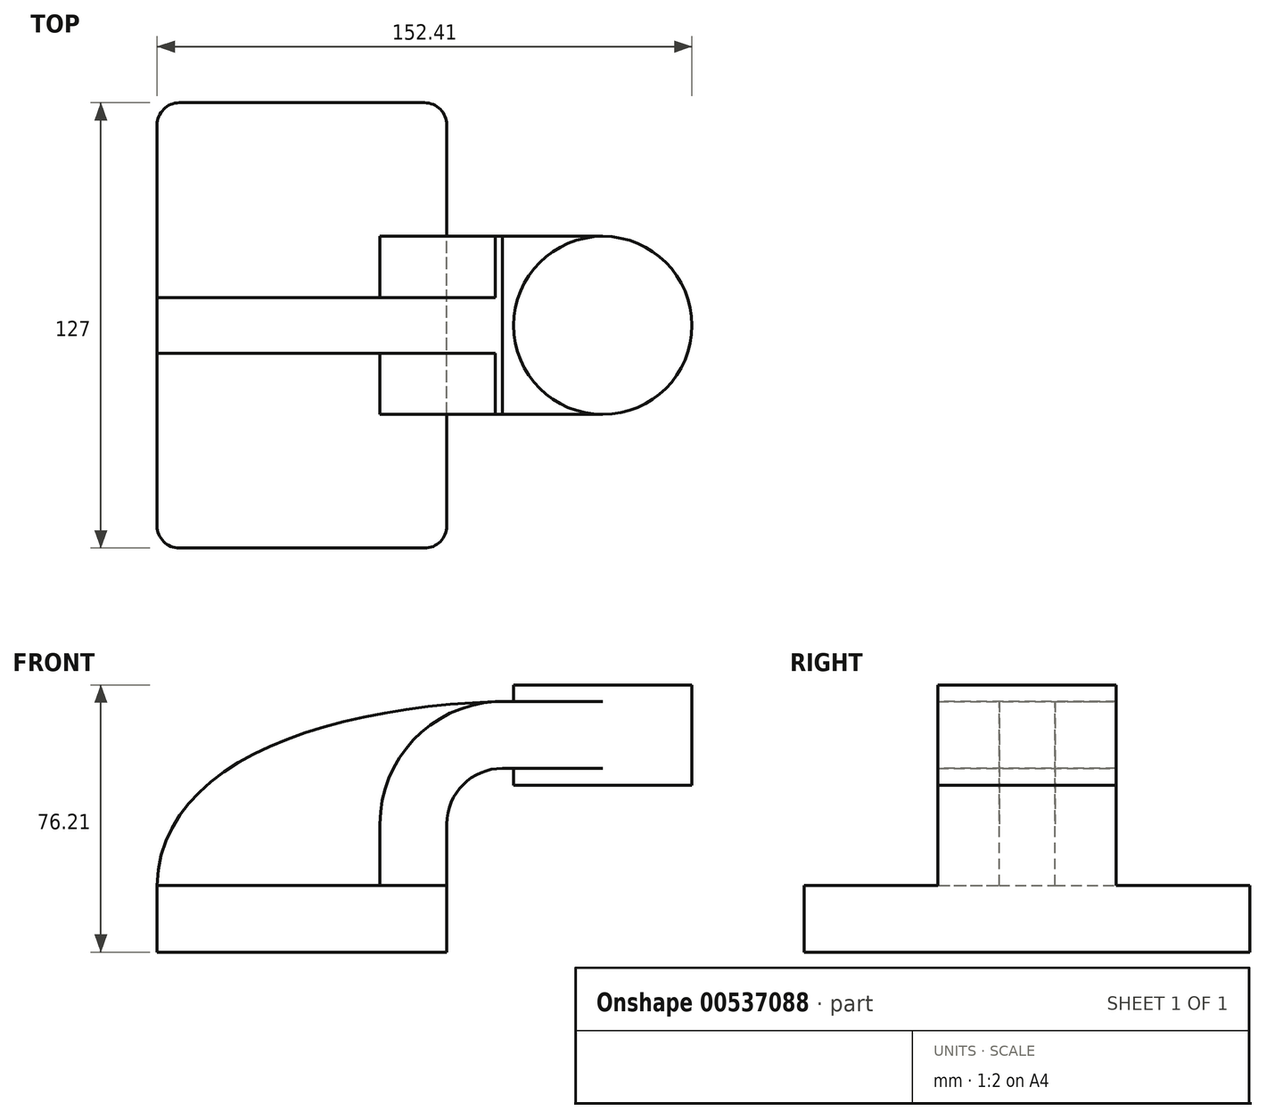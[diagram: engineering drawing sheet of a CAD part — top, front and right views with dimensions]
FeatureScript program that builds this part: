
annotation { "Feature Type Name" : "Feature", "Feature Type Description" : "" }
export const myFeature = defineFeature(function(context is Context, id is Id, definition is map)
    precondition{}
    {
        {
            var Q0;
            Q0=qCreatedBy(makeId("Front.planeOp"),FACE);
            var sketch = newSketch(context, id + "F0", { "sketchPlane" : qUnion([Q0])});
            skLineSegment(sketch, "E0.bottom", {"start": v(41.28, -9.52) * mm, "end": v(-41.28, -9.53) * mm});
            skLineSegment(sketch, "E0.top", {"start": v(41.28, 9.53) * mm, "end": v(-41.28, 9.53) * mm});
            skLineSegment(sketch, "E0.left", {"start": v(41.28, -9.52) * mm, "end": v(41.28, 9.53) * mm});
            skLineSegment(sketch, "E0.right", {"start": v(-41.28, -9.52) * mm, "end": v(-41.28, 9.53) * mm});
            skPoint(sketch, "E0.middle", {"position": v(0, 0) * mm});
            skLineSegment(sketch, "E1.bottom", {"start": v(111.12, 38.1) * mm, "end": v(60.32, 38.1) * mm});
            skLineSegment(sketch, "E1.top", {"start": v(111.12, 66.68) * mm, "end": v(60.32, 66.68) * mm});
            skLineSegment(sketch, "E1.left", {"start": v(111.12, 38.1) * mm, "end": v(111.12, 66.68) * mm});
            skLineSegment(sketch, "E1.right", {"start": v(60.32, 38.1) * mm, "end": v(60.32, 66.68) * mm});
            skPoint(sketch, "E1.middle", {"position": v(85.72, 52.39) * mm});
            skLineSegment(sketch, "E2", {"start": v(41.28, 9.53) * mm, "end": v(41.28, 27) * mm});
            skArc(sketch, "E3", {"start": v(41.27, 27) * mm, "mid": v(45.92, 38.23) * mm, "end": v(57.15, 42.88) * mm});
            skLineSegment(sketch, "E4", {"start": v(57.15, 42.88) * mm, "end": v(85.72, 42.88) * mm});
            skLineSegment(sketch, "E5.0", {"start": v(57.15, 61.93) * mm, "end": v(85.72, 61.93) * mm});
            skArc(sketch, "E5.1", {"start": v(22.23, 27) * mm, "mid": v(32.45, 51.7) * mm, "end": v(57.15, 61.93) * mm});
            skLineSegment(sketch, "E5.2", {"start": v(22.22, 9.53) * mm, "end": v(22.22, 27) * mm});
            skLineSegment(sketch, "E6", {"start": v(85.72, 61.93) * mm, "end": v(85.72, 42.88) * mm});
            skFitSpline(sketch, "E7", {"points": [v(-41.28, 9.53) * mm, v(57.15, 61.93) * mm], "startDerivative": vector(1.89, 105.06) * mm, "endDerivative": vector(151.69, 3.88) * mm});
            skLineSegment(sketch, "E8", {"start": v(85.72, 66.68) * mm, "end": v(85.72, 38.1) * mm});
            skSolve(sketch);
        }
        {
            var Q0;
            Q0=makeQuery(id+"F0.imprint","IMPRINT",FACE,{"disambiguationData":[TD([[makeQuery(id+"F0.imprint","IMPRINT",EDGE,{"derivedFrom":sQuery(id+"F0.wireOp",EDGE,"E0.bottom")}),-1.0]])]});
            extrude(context, id + "F1", {"entities" : qUnion([Q0]), "endBound" : BoundingType.SYMMETRIC, "depth" : 127 * mm, "offsetDistance" : 25.4 * mm});
        }
        {
            var Q0;
            {var subQ3=sQuery(id+"F0.wireOp",EDGE,"E5.2");Q0=makeQuery(id+"F0.imprint","IMPRINT",FACE,{"disambiguationData":[TD([[makeQuery(id+"F0.imprint","IMPRINT",EDGE,{"derivedFrom":subQ3}),1.0]])]});}
            extrude(context, id + "F2", {"entities" : qUnion([Q0]), "operationType" : NewBodyOperationType.ADD, "endBound" : BoundingType.SYMMETRIC, "depth" : 15.88 * mm, "offsetDistance" : 25.4 * mm});
        }
        {
            var Q0;
            {var subQ1=sQuery(id+"F0.wireOp",EDGE,"E2");Q0=makeQuery(id+"F0.imprint","IMPRINT",FACE,{"disambiguationData":[TD([[makeQuery(id+"F0.imprint","IMPRINT",EDGE,{"derivedFrom":subQ1}),1.0]])]});}
            var Q1;
            {var subQ5=sQuery(id+"F0.wireOp",EDGE,"E6");Q1=makeQuery(id+"F0.imprint","IMPRINT",FACE,{"disambiguationData":[TD([[makeQuery(id+"F0.imprint","IMPRINT",EDGE,{"derivedFrom":subQ5}),-1.0]])]});}
            var Q2;
            {var subQ0=sQuery(id+"F0.wireOp",EDGE,"E4");var subQ1=sQuery(id+"F0.wireOp",EDGE,"E1.right");var subQ2=makeQuery(id+"F0.imprint","INTERSECT",VERTEX,{"derivedFrom":[subQ1,subQ0]});Q2=makeQuery(id+"F0.imprint","IMPRINT",FACE,{"disambiguationData":[TD([[makeQuery(id+"F0.imprint","IMPRINT",EDGE,{"disambiguationData":[TD([[subQ2,-1.0]])],"derivedFrom":subQ1}),-1.0]])]});}
            extrude(context, id + "F3", {"entities" : qUnion([Q0, Q1, Q2]), "operationType" : NewBodyOperationType.ADD, "endBound" : BoundingType.SYMMETRIC, "depth" : 50.8 * mm, "offsetDistance" : 25.4 * mm});
        }
        {
            var Q0;
            {var subQ4=sQuery(id+"F0.wireOp",EDGE,"E1.left");Q0=makeQuery(id+"F0.imprint","IMPRINT",FACE,{"disambiguationData":[TD([[makeQuery(id+"F0.imprint","IMPRINT",EDGE,{"derivedFrom":subQ4}),1.0]])]});}
            var Q1;
            Q1=sQuery(id+"F0.wireOp",EDGE,"E8");
            revolve(context, id + "F4", {"operationType" : NewBodyOperationType.ADD, "entities" : qUnion([Q0]), "axis" : qUnion([Q1]), "revolveType" : RevolveType.FULL});
        }
        {
            var Q0;
            Q0=makeQuery(id+"F1.opExtrude","CAP_EDGE",EDGE,{"disambiguationData":[OSD([sQuery(id+"F0.wireOp",EDGE,"E0.right")])],"isStart":false});
            var Q1;
            Q1=makeQuery(id+"F1.opExtrude","CAP_EDGE",EDGE,{"disambiguationData":[OSD([sQuery(id+"F0.wireOp",EDGE,"E0.left")])],"isStart":false});
            var Q2;
            Q2=makeQuery(id+"F1.opExtrude","CAP_EDGE",EDGE,{"disambiguationData":[OSD([sQuery(id+"F0.wireOp",EDGE,"E0.left")])],"isStart":true});
            var Q3;
            Q3=makeQuery(id+"F1.opExtrude","CAP_EDGE",EDGE,{"disambiguationData":[OSD([sQuery(id+"F0.wireOp",EDGE,"E0.right")])],"isStart":true});
            fillet(context, id + "F5", {"entities" : qUnion([Q0, Q1, Q2, Q3]), "radius" : 6.35 * mm, "tangentPropagation" : true, "allowEdgeOverflow" : false});
        }
    });
